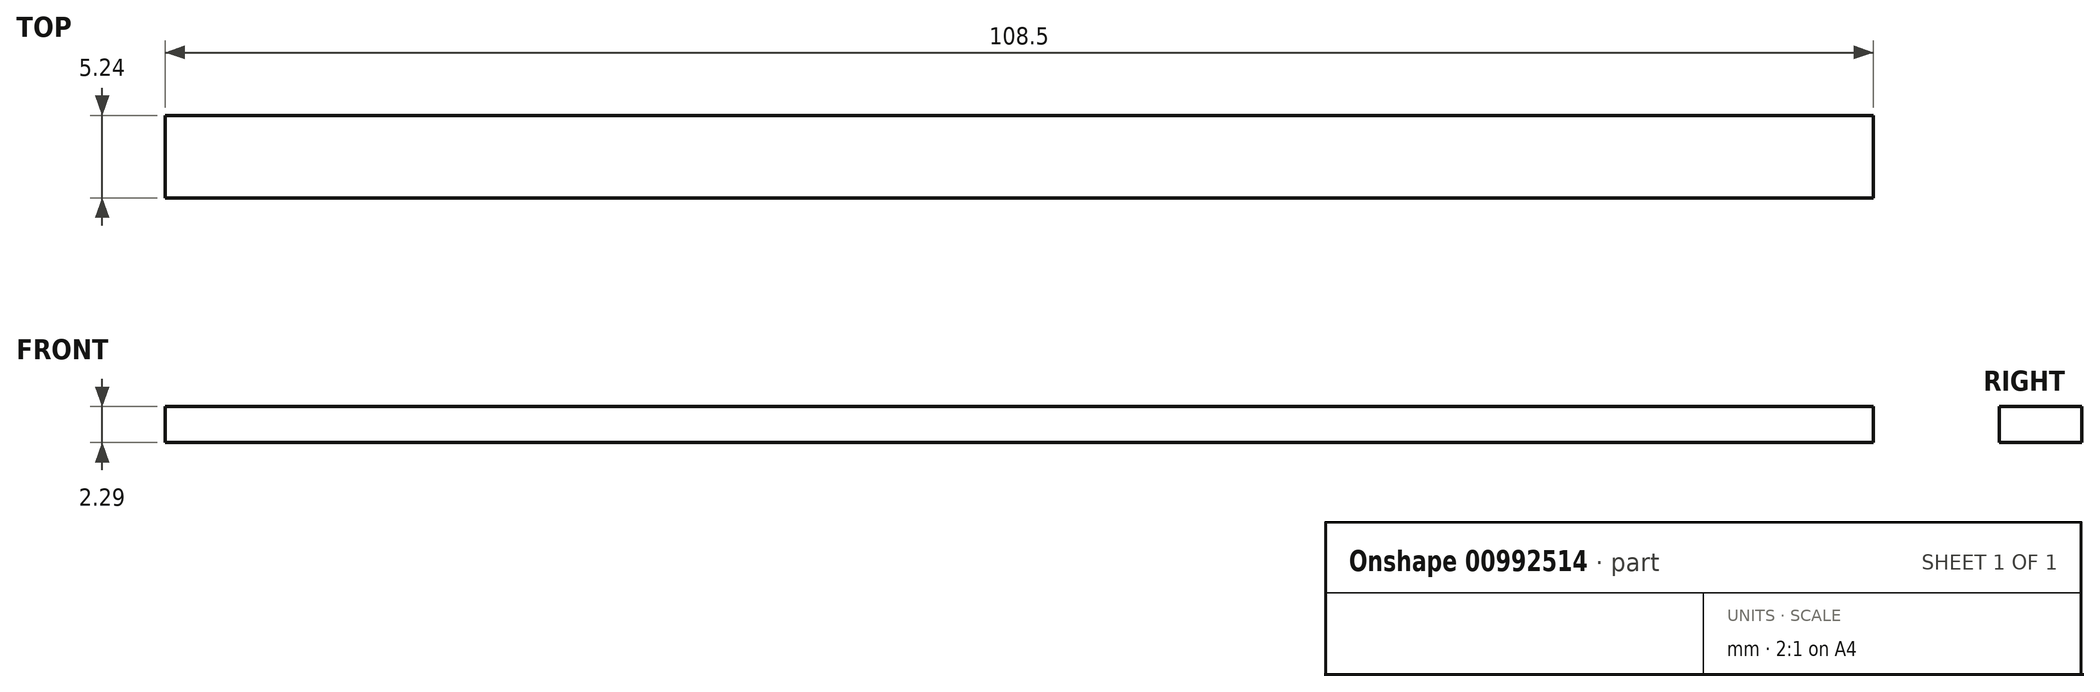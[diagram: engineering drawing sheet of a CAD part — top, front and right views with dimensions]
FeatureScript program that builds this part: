
annotation { "Feature Type Name" : "Feature", "Feature Type Description" : "" }
export const myFeature = defineFeature(function(context is Context, id is Id, definition is map)
    precondition{}
    {
        {
            var Q0;
            Q0=qCreatedBy(makeId("Top.planeOp"),FACE);
            var sketch = newSketch(context, id + "F0", { "sketchPlane" : qUnion([Q0])});
            skLineSegment(sketch, "E0.bottom", {"start": v(-39.68, 49.94) * mm, "end": v(68.82, 49.94) * mm});
            skLineSegment(sketch, "E0.top", {"start": v(-39.68, 44.7) * mm, "end": v(68.82, 44.7) * mm});
            skLineSegment(sketch, "E0.left", {"start": v(-39.68, 49.94) * mm, "end": v(-39.68, 44.7) * mm});
            skLineSegment(sketch, "E0.right", {"start": v(68.82, 49.94) * mm, "end": v(68.82, 44.7) * mm});
            skSolve(sketch);
        }
        {
            var Q0;
            Q0=makeQuery(id+"F0.imprint","IMPRINT",FACE,{"disambiguationData":[TD([[makeQuery(id+"F0.imprint","IMPRINT",EDGE,{"derivedFrom":sQuery(id+"F0.wireOp",EDGE,"E0.bottom")}),-1.0]])]});
            extrude(context, id + "F1", {"entities" : qUnion([Q0]), "depth" : 2.3 * mm, "offsetDistance" : 25.4 * mm});
        }
    });
